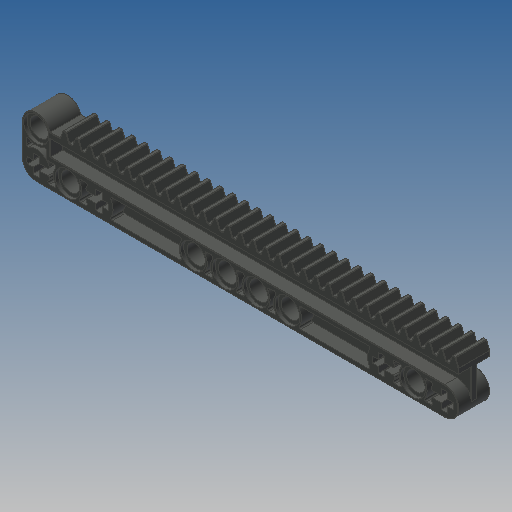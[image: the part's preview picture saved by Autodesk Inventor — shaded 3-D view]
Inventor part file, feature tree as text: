
AUTODESK INVENTOR PART (.ipt)
format: ipt  version: 2022.2 (Build 262287000, 287)  size: 913,920 bytes
history: native  units: in
note: dims shown in document units (in); Inventor stores cm internally (conversion verified against a paired STEP export)
features: extrude x4, fillet x2, sketch x1, pattern_linear x1
ambient origin geometry x8: Origin, YZ Plane, XZ Plane, XY Plane, X Axis, Y Axis, Z Axis, Center Point
bodies: Solid1 (feature_tree)
feature tree (8):
  sketch  "Sketch2"  dims[d0=0.315in d1=0.2835in d2=0.9449in d3=0.252in d4=0.189in d5=0.0551in d6=0.4961in d7=0.0787in d8=0.0945in d9=0.0315in d10=45.0deg d11=0.063in d12=0.063in d13=0.063in d14=0.063in d15=0.315in d16=0.0in d17=0.252in d18=0.0in d19=0.063in d20=0.0in d21=0.315in d22=0.0in d23=0.0039in d24=12.5984in d26=0.126in d27=0.0039in d28=0.0157in]
  extrude  "Extrusion1"  Depth=0.0157in
  extrude  "Extrusion2"  Depth=0.0157in
  extrude  "Extrusion3"  Depth=0.0157in
  extrude  "Extrusion4"  Depth=0.0157in
  fillet  "Fillet1"  Radius=0.0551in
  pattern_linear  "Rectangular Pattern1"  Spacing1=0.4961in  [1 undecoded]
  fillet  "Fillet2"  Radius=0.0787in
note: 1 required parameter value undecoded (feature->parameter linkage not recoverable at this tier; creation-order binding heuristic only, values carry confidence <= 0.55)
